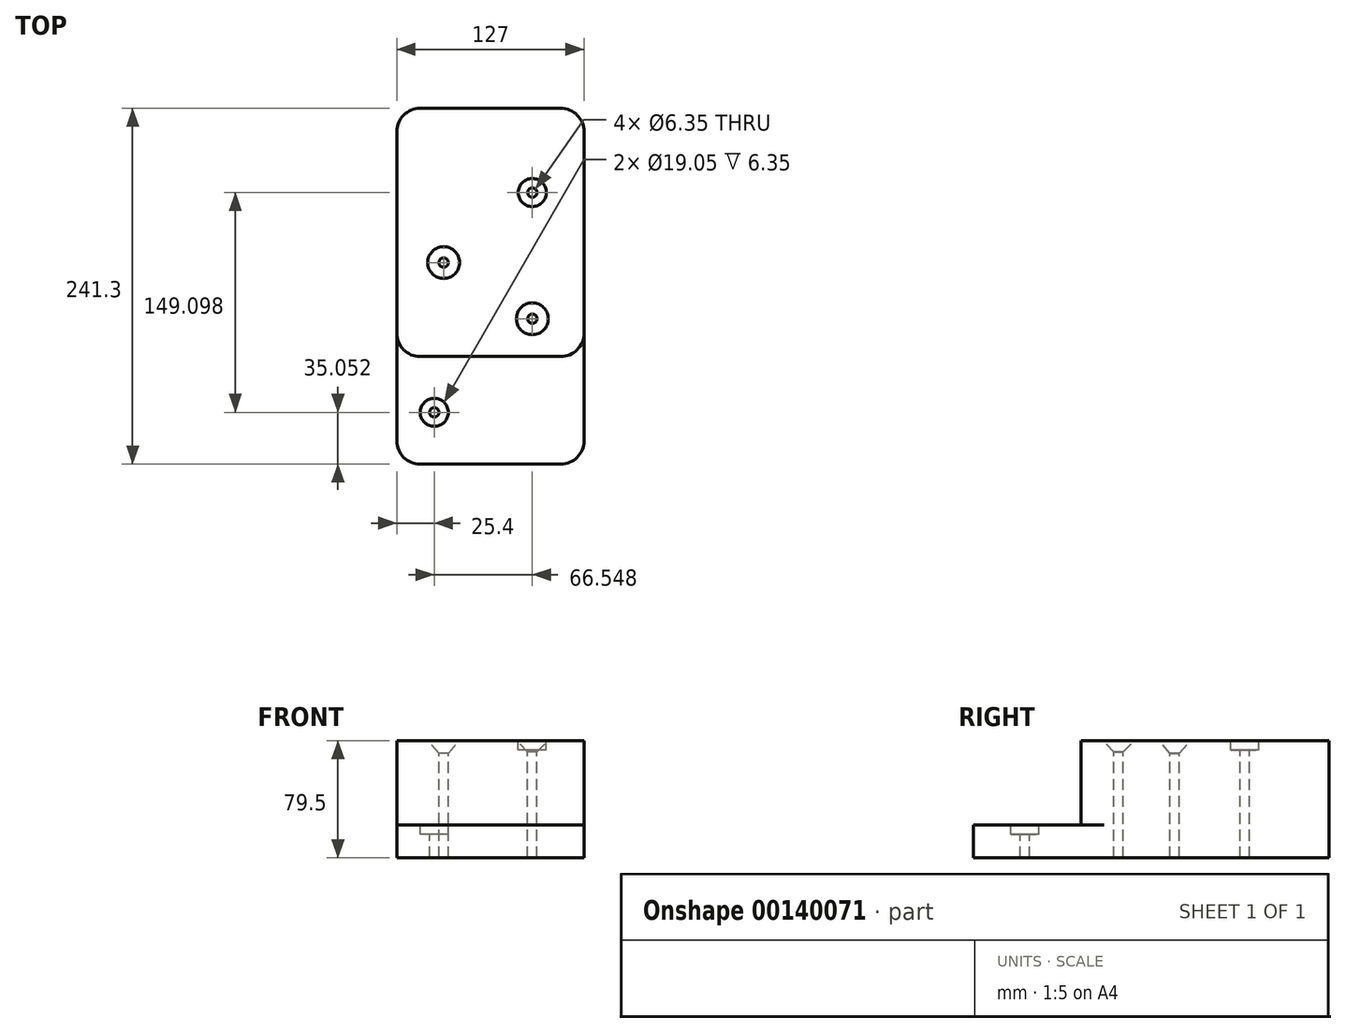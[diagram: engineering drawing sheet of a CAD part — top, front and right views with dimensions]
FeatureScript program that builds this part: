
annotation { "Feature Type Name" : "Feature", "Feature Type Description" : "" }
export const myFeature = defineFeature(function(context is Context, id is Id, definition is map)
    precondition{}
    {
        {
            var Q0;
            Q0=qCreatedBy(makeId("Right.planeOp"),FACE);
            var sketch = newSketch(context, id + "F0", { "sketchPlane" : qUnion([Q0])});
            skLineSegment(sketch, "E0.bottom", {"start": v(0, 0) * mm, "end": v(241.3, 0) * mm});
            skLineSegment(sketch, "E0.top", {"start": v(0, 22.35) * mm, "end": v(241.3, 22.35) * mm});
            skLineSegment(sketch, "E0.left", {"start": v(0, 0) * mm, "end": v(0, 22.35) * mm});
            skLineSegment(sketch, "E0.right", {"start": v(241.3, 0) * mm, "end": v(241.3, 22.35) * mm});
            skSolve(sketch);
        }
        {
            var Q0;
            Q0 = qSketchRegion(id + "F0", true);
            extrude(context, id + "F1", {"entities" : qUnion([Q0]), "oppositeDirection" : true, "depth" : 127 * mm});
        }
        {
            var Q0;
            Q0=makeQuery(id+"F1.opExtrude","CAP_EDGE",EDGE,{"disambiguationData":[OSD([sQuery(id+"F0.wireOp",EDGE,"E0.left")])],"isStart":true});
            var Q1;
            Q1=makeQuery(id+"F1.opExtrude","CAP_EDGE",EDGE,{"disambiguationData":[OSD([sQuery(id+"F0.wireOp",EDGE,"E0.left")])],"isStart":false});
            fillet(context, id + "F2", {"entities" : qUnion([Q0, Q1]), "radius" : 15.75 * mm, "tangentPropagation" : true, "allowEdgeOverflow" : false});
        }
        {
            var Q0;
            Q0=makeQuery(id+"F1.opExtrude","SWEPT_FACE",FACE,{"disambiguationData":[OSD([sQuery(id+"F0.wireOp",EDGE,"E0.top")])]});
            var sketch = newSketch(context, id + "F3", { "sketchPlane" : qUnion([Q0])});
            skLineSegment(sketch, "E1.bottom", {"start": v(0, 72.9) * mm, "end": v(-127, 72.9) * mm});
            skLineSegment(sketch, "E1.top", {"start": v(0, 241.3) * mm, "end": v(-127, 241.3) * mm});
            skLineSegment(sketch, "E1.left", {"start": v(0, 72.9) * mm, "end": v(0, 241.3) * mm});
            skLineSegment(sketch, "E1.right", {"start": v(-127, 72.9) * mm, "end": v(-127, 241.3) * mm});
            skSolve(sketch);
        }
        {
            var Q0;
            Q0 = qSketchRegion(id + "F3", true);
            extrude(context, id + "F4", {"entities" : qUnion([Q0]), "operationType" : NewBodyOperationType.ADD, "depth" : 57.15 * mm});
        }
        {
            var Q0;
            Q0=makeQuery(id+"F4.opExtrude","SWEPT_EDGE",EDGE,{"disambiguationData":[OSD([sQuery(id+"F0.wireOp",EDGE,"E0.top"),sQuery(id+"F3.wireOp",EDGE,"E1.bottom"),sQuery(id+"F3.wireOp",EDGE,"E1.left")])]});
            var Q1;
            Q1=makeQuery(id+"F4.opExtrude","SWEPT_EDGE",EDGE,{"disambiguationData":[OSD([sQuery(id+"F0.wireOp",EDGE,"E0.top"),sQuery(id+"F3.wireOp",EDGE,"E1.bottom"),sQuery(id+"F3.wireOp",EDGE,"E1.right")])]});
            var Q2;
            Q2=makeQuery(id+"F4.boolean.opBoolean","MERGE",EDGE,{"derivedFrom":[makeQuery(id+"F1.opExtrude","CAP_EDGE",EDGE,{"disambiguationData":[OSD([sQuery(id+"F0.wireOp",EDGE,"E0.right")])],"isStart":true}),makeQuery(id+"F4.opExtrude","SWEPT_EDGE",EDGE,{"disambiguationData":[OSD([sQuery(id+"F3.wireOp",EDGE,"E1.top"),sQuery(id+"F3.wireOp",EDGE,"E1.left")])]})]});
            var Q3;
            Q3=makeQuery(id+"F4.boolean.opBoolean","MERGE",EDGE,{"derivedFrom":[makeQuery(id+"F1.opExtrude","CAP_EDGE",EDGE,{"disambiguationData":[OSD([sQuery(id+"F0.wireOp",EDGE,"E0.right")])],"isStart":false}),makeQuery(id+"F4.opExtrude","SWEPT_EDGE",EDGE,{"disambiguationData":[OSD([sQuery(id+"F3.wireOp",EDGE,"E1.top"),sQuery(id+"F3.wireOp",EDGE,"E1.right")])]})]});
            fillet(context, id + "F5", {"entities" : qUnion([Q0, Q1, Q2, Q3]), "radius" : 15.75 * mm, "tangentPropagation" : true, "allowEdgeOverflow" : false});
        }
        {
            var Q0;
            Q0=makeQuery(id+"F1.opExtrude","SWEPT_FACE",FACE,{"disambiguationData":[OSD([sQuery(id+"F0.wireOp",EDGE,"E0.top")])]});
            var sketch = newSketch(context, id + "F6", { "sketchPlane" : qUnion([Q0])});
            skCircle(sketch, "E2", {"center": v(-101.6, 35.05) * mm, "radius": 9.53 * mm});
            skSolve(sketch);
        }
        {
            var Q0;
            Q0=sQuery(id+"F6.wireOp",VERTEX,"E2.center");
            var Q1;
            Q1=makeQuery(id+"F1.opExtrude","SWEPT_BODY",BODY,{"disambiguationData":[OSD([sQuery(id+"F0.wireOp",EDGE,"E0.bottom"),sQuery(id+"F0.wireOp",EDGE,"E0.top"),sQuery(id+"F0.wireOp",EDGE,"E0.left"),sQuery(id+"F0.wireOp",EDGE,"E0.right")])]});
            hole(context, id + "F7", {"style" : HoleStyle.C_BORE, "endStyle" : HoleEndStyle.THROUGH, "holeDiameter" : 6.35 * mm, "cBoreDiameter" : 19.05 * mm, "cBoreDepth" : 6.35 * mm, "locations" : qUnion([Q0]), "scope" : qUnion([Q1]), "isTappedThrough" : true});
        }
        {
            var Q0;
            Q0=makeQuery(id+"F4.opExtrude","CAP_FACE",FACE,{"disambiguationData":[OSD([sQuery(id+"F3.wireOp",EDGE,"E1.bottom"),sQuery(id+"F3.wireOp",EDGE,"E1.top"),sQuery(id+"F3.wireOp",EDGE,"E1.left"),sQuery(id+"F3.wireOp",EDGE,"E1.right")])],"isStart":false});
            var sketch = newSketch(context, id + "F8", { "sketchPlane" : qUnion([Q0])});
            skCircle(sketch, "E3", {"center": v(-95.25, 136.65) * mm, "radius": 9.53 * mm, "construction": true});
            skCircle(sketch, "E4", {"center": v(-35.05, 98.55) * mm, "radius": 9.53 * mm, "construction": true});
            skCircle(sketch, "E5", {"center": v(-35.05, 184.15) * mm, "radius": 9.53 * mm, "construction": true});
            skSolve(sketch);
        }
        {
            var Q0;
            Q0=sQuery(id+"F8.wireOp",VERTEX,"E3.center");
            var Q1;
            Q1=makeQuery(id+"F1.opExtrude","SWEPT_BODY",BODY,{"disambiguationData":[OSD([sQuery(id+"F0.wireOp",EDGE,"E0.bottom"),sQuery(id+"F0.wireOp",EDGE,"E0.top"),sQuery(id+"F0.wireOp",EDGE,"E0.left"),sQuery(id+"F0.wireOp",EDGE,"E0.right")])]});
            hole(context, id + "F9", {"style" : HoleStyle.C_SINK, "endStyle" : HoleEndStyle.THROUGH, "holeDiameter" : 6.35 * mm, "cSinkDiameter" : 21.59 * mm, "cSinkAngle" : 82 * degree, "locations" : qUnion([Q0]), "scope" : qUnion([Q1]), "isTappedThrough" : true});
        }
        {
            var Q0;
            Q0=sQuery(id+"F8.wireOp",VERTEX,"E4.center");
            var Q1;
            Q1=makeQuery(id+"F1.opExtrude","SWEPT_BODY",BODY,{"disambiguationData":[OSD([sQuery(id+"F0.wireOp",EDGE,"E0.bottom"),sQuery(id+"F0.wireOp",EDGE,"E0.top"),sQuery(id+"F0.wireOp",EDGE,"E0.left"),sQuery(id+"F0.wireOp",EDGE,"E0.right")])]});
            hole(context, id + "F10", {"style" : HoleStyle.C_SINK, "endStyle" : HoleEndStyle.THROUGH, "holeDiameter" : 6.35 * mm, "cSinkDiameter" : 21.59 * mm, "cSinkAngle" : 90 * degree, "locations" : qUnion([Q0]), "scope" : qUnion([Q1]), "isTappedThrough" : true});
        }
        {
            var Q0;
            Q0=sQuery(id+"F8.wireOp",VERTEX,"E5.center");
            var Q1;
            Q1=makeQuery(id+"F1.opExtrude","SWEPT_BODY",BODY,{"disambiguationData":[OSD([sQuery(id+"F0.wireOp",EDGE,"E0.bottom"),sQuery(id+"F0.wireOp",EDGE,"E0.top"),sQuery(id+"F0.wireOp",EDGE,"E0.left"),sQuery(id+"F0.wireOp",EDGE,"E0.right")])]});
            hole(context, id + "F11", {"style" : HoleStyle.C_BORE, "endStyle" : HoleEndStyle.THROUGH, "holeDiameter" : 6.35 * mm, "cBoreDiameter" : 19.05 * mm, "cBoreDepth" : 6.35 * mm, "locations" : qUnion([Q0]), "scope" : qUnion([Q1]), "isTappedThrough" : true});
        }
    });
